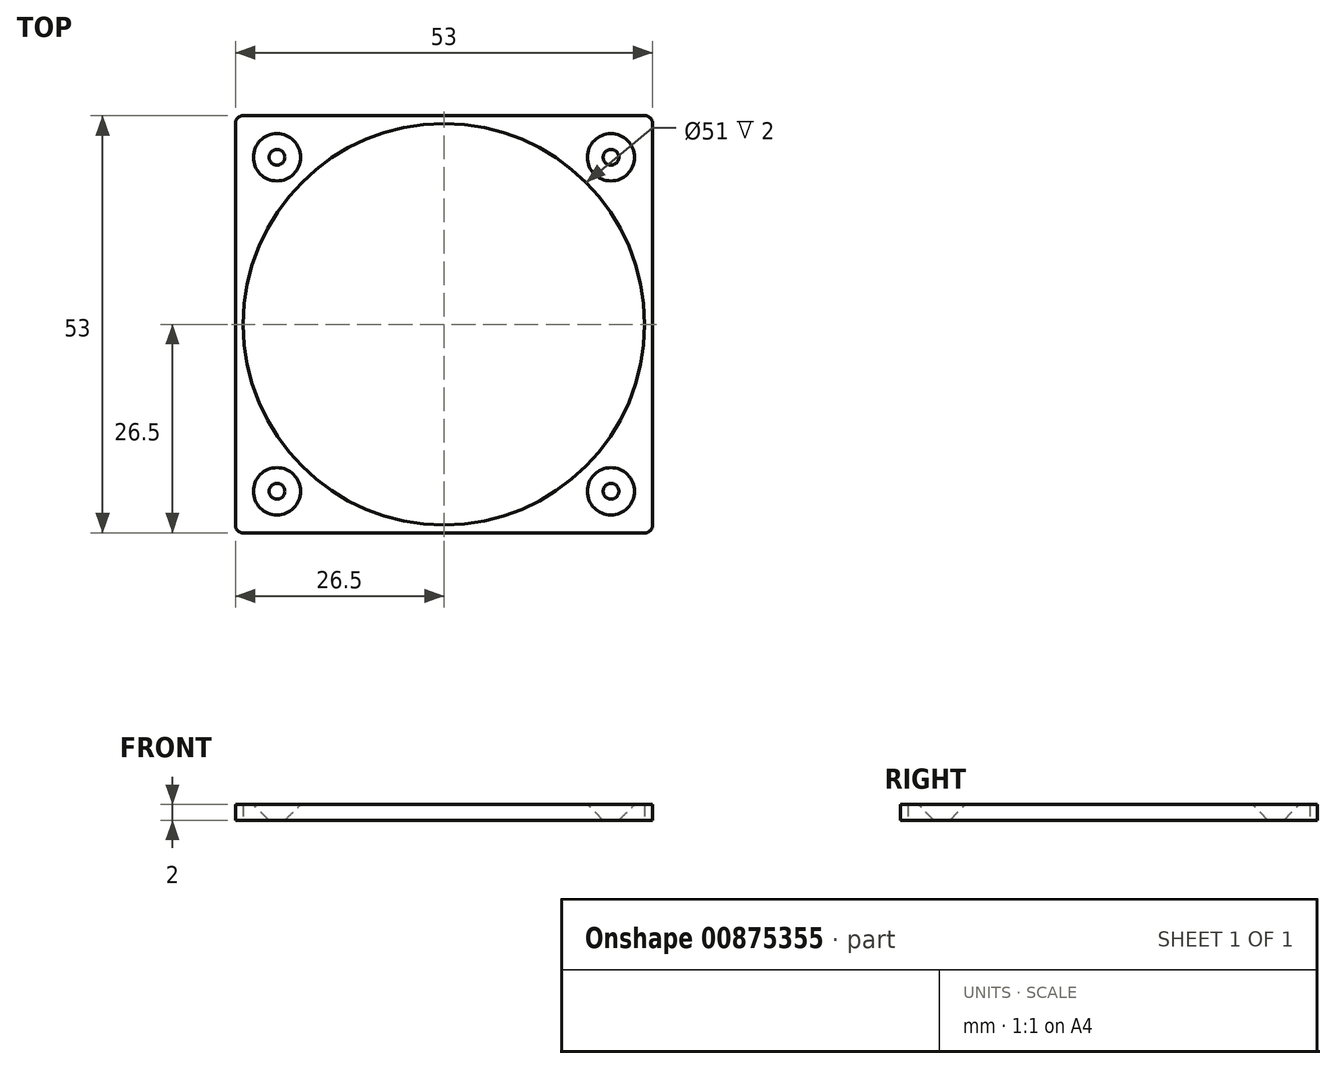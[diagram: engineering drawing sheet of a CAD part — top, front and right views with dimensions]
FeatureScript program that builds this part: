
annotation { "Feature Type Name" : "Feature", "Feature Type Description" : "" }
export const myFeature = defineFeature(function(context is Context, id is Id, definition is map)
    precondition{}
    {
        {
            var Q0;
            Q0=qCreatedBy(makeId("Top.planeOp"),FACE);
            var sketch = newSketch(context, id + "F0", { "sketchPlane" : qUnion([Q0])});
            skCircle(sketch, "E0", {"center": v(0, 0) * mm, "radius": 25.5 * mm});
            skLineSegment(sketch, "E1.bottom", {"start": v(26.5, -26.5) * mm, "end": v(-26.5, -26.5) * mm});
            skLineSegment(sketch, "E1.top", {"start": v(26.5, 26.5) * mm, "end": v(-26.5, 26.5) * mm});
            skLineSegment(sketch, "E1.left", {"start": v(26.5, -26.5) * mm, "end": v(26.5, 26.5) * mm});
            skLineSegment(sketch, "E1.right", {"start": v(-26.5, -26.5) * mm, "end": v(-26.5, 26.5) * mm});
            skLineSegment(sketch, "E2", {"start": v(-26.5, 26.5) * mm, "end": v(26.5, -26.5) * mm, "construction": true});
            skLineSegment(sketch, "E3", {"start": v(26.5, 26.5) * mm, "end": v(-26.5, -26.5) * mm, "construction": true});
            skCircle(sketch, "E4", {"center": v(-21.21, 21.21) * mm, "radius": 1 * mm});
            skCircle(sketch, "E5", {"center": v(21.21, 21.21) * mm, "radius": 1 * mm});
            skCircle(sketch, "E6", {"center": v(21.21, -21.21) * mm, "radius": 1 * mm});
            skCircle(sketch, "E7", {"center": v(-21.21, -21.21) * mm, "radius": 1 * mm});
            skSolve(sketch);
        }
        {
            var Q0;
            Q0=makeQuery(id+"F0.imprint","IMPRINT",FACE,{"disambiguationData":[TD([[makeQuery(id+"F0.imprint","IMPRINT",EDGE,{"derivedFrom":sQuery(id+"F0.wireOp",EDGE,"E0")}),-1.0]])]});
            extrude(context, id + "F1", {"entities" : qUnion([Q0]), "depth" : 2 * mm, "offsetDistance" : 25 * mm});
        }
        {
            var Q0;
            Q0=makeQuery(id+"F1.opExtrude","CAP_EDGE",EDGE,{"disambiguationData":[OSD([sQuery(id+"F0.wireOp",EDGE,"E4")])],"isStart":false});
            var Q1;
            Q1=makeQuery(id+"F1.opExtrude","CAP_EDGE",EDGE,{"disambiguationData":[OSD([sQuery(id+"F0.wireOp",EDGE,"E5")])],"isStart":false});
            var Q2;
            Q2=makeQuery(id+"F1.opExtrude","CAP_EDGE",EDGE,{"disambiguationData":[OSD([sQuery(id+"F0.wireOp",EDGE,"E6")])],"isStart":false});
            var Q3;
            Q3=makeQuery(id+"F1.opExtrude","CAP_EDGE",EDGE,{"disambiguationData":[OSD([sQuery(id+"F0.wireOp",EDGE,"E7")])],"isStart":false});
            chamfer(context, id + "F2", {"entities" : qUnion([Q0, Q1, Q2, Q3]), "width" : 2 * mm, "tangentPropagation" : true});
        }
        {
            var Q0;
            Q0=makeQuery(id+"F1.opExtrude","SWEPT_EDGE",EDGE,{"disambiguationData":[OSD([sQuery(id+"F0.wireOp",EDGE,"E1.bottom"),sQuery(id+"F0.wireOp",EDGE,"E1.left")])]});
            var Q1;
            Q1=makeQuery(id+"F1.opExtrude","SWEPT_EDGE",EDGE,{"disambiguationData":[OSD([sQuery(id+"F0.wireOp",EDGE,"E1.top"),sQuery(id+"F0.wireOp",EDGE,"E1.left")])]});
            var Q2;
            Q2=makeQuery(id+"F1.opExtrude","SWEPT_EDGE",EDGE,{"disambiguationData":[OSD([sQuery(id+"F0.wireOp",EDGE,"E1.bottom"),sQuery(id+"F0.wireOp",EDGE,"E1.right")])]});
            var Q3;
            Q3=makeQuery(id+"F1.opExtrude","SWEPT_EDGE",EDGE,{"disambiguationData":[OSD([sQuery(id+"F0.wireOp",EDGE,"E1.top"),sQuery(id+"F0.wireOp",EDGE,"E1.right")])]});
            fillet(context, id + "F3", {"entities" : qUnion([Q0, Q1, Q2, Q3]), "radius" : 1 * mm, "tangentPropagation" : true, "allowEdgeOverflow" : false});
        }
    });
